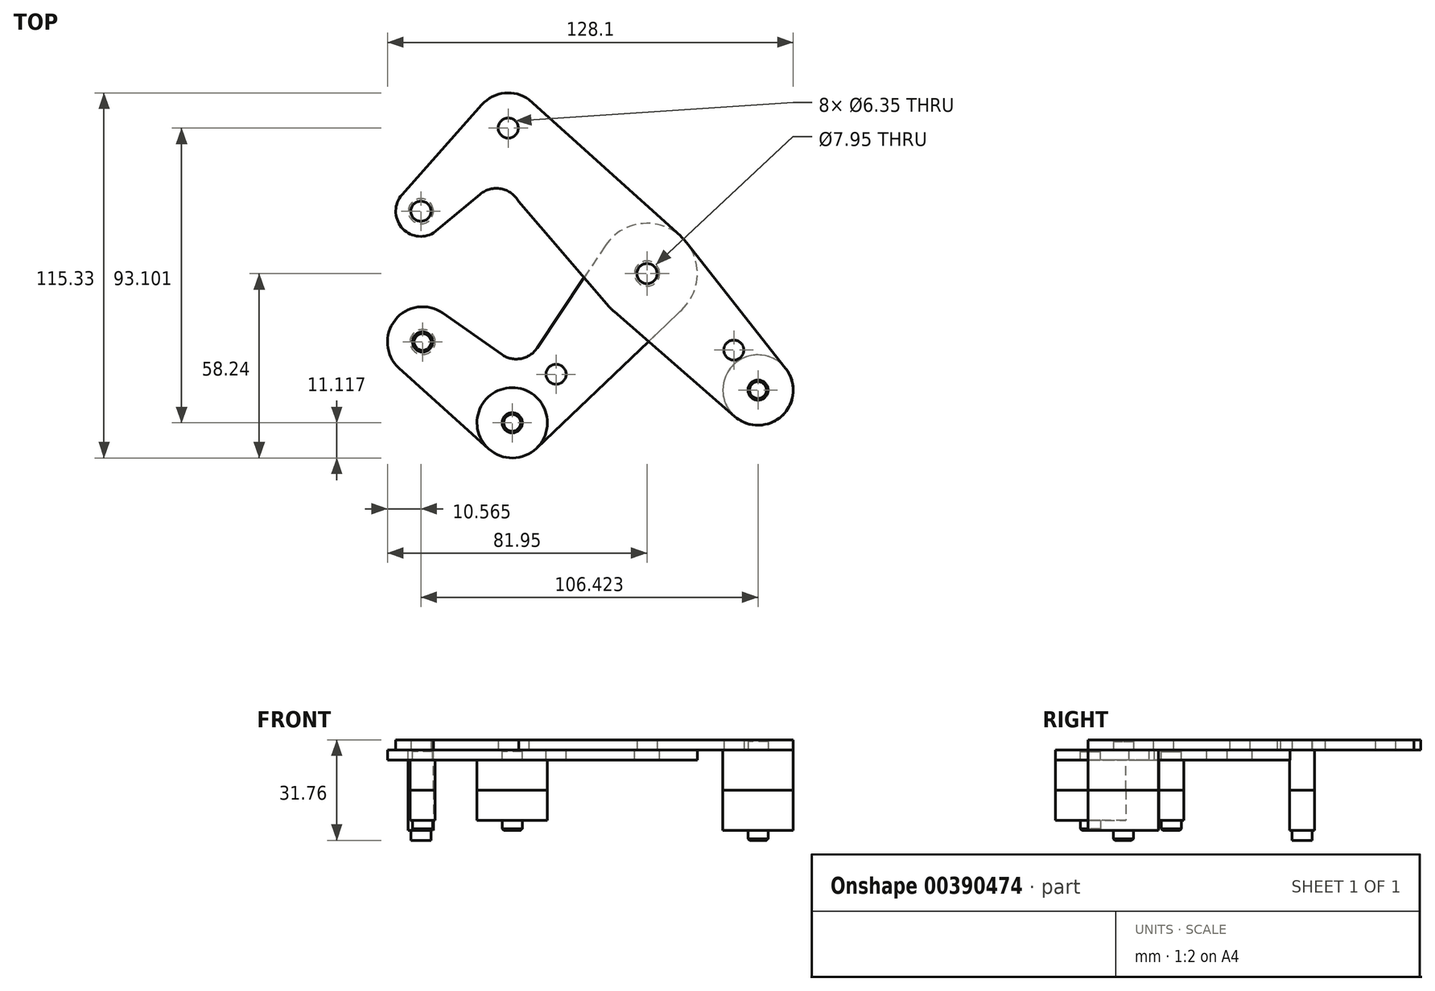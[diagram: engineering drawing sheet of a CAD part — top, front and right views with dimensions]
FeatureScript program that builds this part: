
annotation { "Feature Type Name" : "Feature", "Feature Type Description" : "" }
export const myFeature = defineFeature(function(context is Context, id is Id, definition is map)
    precondition{}
    {
        {
            var Q0;
            Q0=qCreatedBy(makeId("Top.planeOp"),FACE);
            var sketch = newSketch(context, id + "F0", { "sketchPlane" : qUnion([Q0])});
            skCircle(sketch, "E0", {"center": v(0, 0) * mm, "radius": 15.88 * mm});
            skCircle(sketch, "E1", {"center": v(0, 0) * mm, "radius": 3.18 * mm});
            skLineSegment(sketch, "E2", {"start": v(-50.22, 52.72) * mm, "end": v(58.42, -61.33) * mm, "construction": true});
            skLineSegment(sketch, "E3", {"start": v(-26.19, 62.75) * mm, "end": v(-73.55, 17.64) * mm, "construction": true});
            skCircle(sketch, "E4", {"center": v(-71.38, 19.7) * mm, "radius": 7.94 * mm});
            skCircle(sketch, "E5", {"center": v(-43.8, 45.98) * mm, "radius": 11.11 * mm});
            skCircle(sketch, "E6", {"center": v(35.04, -36.78) * mm, "radius": 11.11 * mm});
            skCircle(sketch, "E7", {"center": v(-43.8, 45.98) * mm, "radius": 3.18 * mm});
            skCircle(sketch, "E8", {"center": v(35.04, -36.78) * mm, "radius": 3.18 * mm});
            skCircle(sketch, "E9", {"center": v(-71.38, 19.7) * mm, "radius": 3.18 * mm});
            skCircle(sketch, "E10", {"center": v(0, 0) * mm, "radius": 3.98 * mm});
            skLineSegment(sketch, "E11", {"start": v(43.77, -29.9) * mm, "end": v(12.47, 9.82) * mm});
            skLineSegment(sketch, "E12", {"start": v(12.47, 9.82) * mm, "end": v(12.47, 9.82) * mm});
            skLineSegment(sketch, "E13", {"start": v(-52.1, 53.36) * mm, "end": v(-77.32, 24.97) * mm});
            skLineSegment(sketch, "E14", {"start": v(-37.25, 54.96) * mm, "end": v(10.63, 11.8) * mm});
            skLineSegment(sketch, "E15", {"start": v(-12.03, -10.36) * mm, "end": v(-40.55, 22.75) * mm});
            skLineSegment(sketch, "E16", {"start": v(-67.37, 12.85) * mm, "end": v(-52.63, 25.1) * mm});
            skArc(sketch, "E17", {"start": v(-52.63, 25.1) * mm, "mid": v(-46.04, 26.78) * mm, "end": v(-40.55, 22.75) * mm});
            skLineSegment(sketch, "E18", {"start": v(-10.42, -11.98) * mm, "end": v(27.75, -45.17) * mm});
            skLineSegment(sketch, "E19", {"start": v(0, 0) * mm, "end": v(-50.8, -56.24) * mm, "construction": true});
            skLineSegment(sketch, "E20", {"start": v(-35.24, -53.73) * mm, "end": v(-80.55, -12.81) * mm, "construction": true});
            skCircle(sketch, "E21", {"center": v(-70.84, -21.58) * mm, "radius": 3.18 * mm});
            skCircle(sketch, "E22", {"center": v(-70.84, -21.58) * mm, "radius": 11.11 * mm});
            skCircle(sketch, "E23", {"center": v(-42.56, -47.12) * mm, "radius": 3.18 * mm});
            skCircle(sketch, "E24", {"center": v(-42.56, -47.12) * mm, "radius": 11.11 * mm});
            skCircle(sketch, "E25", {"center": v(-28.72, -31.8) * mm, "radius": 3.18 * mm});
            skLineSegment(sketch, "E26", {"start": v(-64.46, -12.48) * mm, "end": v(-45.8, -25.56) * mm});
            skLineSegment(sketch, "E27", {"start": v(-79.53, -28.7) * mm, "end": v(-50.01, -55.37) * mm});
            skLineSegment(sketch, "E28", {"start": v(-34.9, -55.17) * mm, "end": v(10.95, -11.5) * mm});
            skLineSegment(sketch, "E29", {"start": v(-13.22, 8.78) * mm, "end": v(-34.62, -23.44) * mm});
            skArc(sketch, "E30", {"start": v(-45.8, -25.56) * mm, "mid": v(-39.77, -26.86) * mm, "end": v(-34.62, -23.44) * mm});
            skCircle(sketch, "E31", {"center": v(27.4, -24.16) * mm, "radius": 3.18 * mm});
            skPoint(sketch, "E31.first.point", {"position": v(25.2, -26.45) * mm});
            skPoint(sketch, "E31.second.point", {"position": v(29.75, -22.03) * mm});
            skPoint(sketch, "E31.third.point", {"position": v(30.07, -25.87) * mm});
            skSolve(sketch);
        }
        {
            var Q0;
            Q0=qCreatedBy(makeId("Top.planeOp"),FACE);
            cPlane(context, id + "F1", {"entities" : qUnion([Q0]), "cplaneType" : CPlaneType.OFFSET, "offset" : 12.7 * mm, "oppositeDirection" : true, "width" : 152.4 * mm, "height" : 152.4 * mm});
        }
        {
            var Q0;
            {var subQ0=sQuery(id+"F0.wireOp",EDGE,"E16");var subQ1=sQuery(id+"F0.wireOp",EDGE,"E4");var subQ2=makeQuery(id+"F0.imprint","INTERSECT",VERTEX,{"disambiguationData":[OD(0.0)],"derivedFrom":[subQ1,subQ0]});Q0=makeQuery(id+"F0.imprint","IMPRINT",FACE,{"disambiguationData":[TD([[makeQuery(id+"F0.imprint","IMPRINT",EDGE,{"disambiguationData":[TD([[subQ2,-1.0]])],"derivedFrom":subQ1}),1.0]])]});}
            var Q1;
            {var subQ0=sQuery(id+"F0.wireOp",EDGE,"E14");var subQ1=sQuery(id+"F0.wireOp",EDGE,"E5");var subQ2=makeQuery(id+"F0.imprint","INTERSECT",VERTEX,{"disambiguationData":[OD(0.0)],"derivedFrom":[subQ1,subQ0]});Q1=makeQuery(id+"F0.imprint","IMPRINT",FACE,{"disambiguationData":[TD([[makeQuery(id+"F0.imprint","IMPRINT",EDGE,{"disambiguationData":[TD([[subQ2,1.0]])],"derivedFrom":subQ1}),1.0]])]});}
            var Q2;
            Q2=makeQuery(id+"F0.imprint","IMPRINT",FACE,{"disambiguationData":[TD([[makeQuery(id+"F0.imprint","IMPRINT",EDGE,{"derivedFrom":sQuery(id+"F0.wireOp",EDGE,"E8")}),-1.0]])]});
            var Q3;
            {var subQ0=sQuery(id+"F0.wireOp",EDGE,"E15");var subQ1=sQuery(id+"F0.wireOp",EDGE,"E0");var subQ2=makeQuery(id+"F0.imprint","INTERSECT",VERTEX,{"derivedFrom":[subQ1,subQ0]});Q3=makeQuery(id+"F0.imprint","IMPRINT",FACE,{"disambiguationData":[TD([[makeQuery(id+"F0.imprint","IMPRINT",EDGE,{"disambiguationData":[TD([[subQ2,1.0]])],"derivedFrom":subQ1}),-1.0]])]});}
            var Q4;
            {var subQ0=sQuery(id+"F0.wireOp",EDGE,"E18");var subQ1=sQuery(id+"F0.wireOp",EDGE,"E0");var subQ2=makeQuery(id+"F0.imprint","INTERSECT",VERTEX,{"derivedFrom":[subQ1,subQ0]});Q4=makeQuery(id+"F0.imprint","IMPRINT",FACE,{"disambiguationData":[TD([[makeQuery(id+"F0.imprint","IMPRINT",EDGE,{"disambiguationData":[TD([[subQ2,-1.0]])],"derivedFrom":subQ1}),-1.0]])]});}
            var Q5;
            Q5=makeQuery(id+"F0.imprint","IMPRINT",FACE,{"disambiguationData":[TD([[makeQuery(id+"F0.imprint","IMPRINT",EDGE,{"derivedFrom":sQuery(id+"F0.wireOp",EDGE,"E9")}),-1.0]])]});
            var Q6;
            Q6=makeQuery(id+"F0.imprint","IMPRINT",FACE,{"disambiguationData":[TD([[makeQuery(id+"F0.imprint","IMPRINT",EDGE,{"derivedFrom":sQuery(id+"F0.wireOp",EDGE,"E7")}),-1.0]])]});
            var Q7;
            {var subQ0=sQuery(id+"F0.wireOp",EDGE,"E13");Q7=makeQuery(id+"F0.imprint","IMPRINT",FACE,{"disambiguationData":[TD([[makeQuery(id+"F0.imprint","IMPRINT",EDGE,{"derivedFrom":subQ0}),1.0]])]});}
            var Q8;
            {var subQ7=sQuery(id+"F0.wireOp",EDGE,"E11");Q8=makeQuery(id+"F0.imprint","IMPRINT",FACE,{"disambiguationData":[TD([[makeQuery(id+"F0.imprint","IMPRINT",EDGE,{"derivedFrom":subQ7}),1.0]])]});}
            var Q9;
            Q9=makeQuery(id+"F0.imprint","IMPRINT",FACE,{"disambiguationData":[TD([[makeQuery(id+"F0.imprint","IMPRINT",EDGE,{"derivedFrom":sQuery(id+"F0.wireOp",EDGE,"E10")}),-1.0]])]});
            var Q10;
            Q10=makeQuery(id+"F0.imprint","IMPRINT",FACE,{"disambiguationData":[TD([[makeQuery(id+"F0.imprint","IMPRINT",EDGE,{"derivedFrom":sQuery(id+"F0.wireOp",EDGE,"E1")}),-1.0]])]});
            extrude(context, id + "F2", {"entities" : qUnion([Q0, Q1, Q2, Q3, Q4, Q5, Q6, Q7, Q8, Q9, Q10]), "depth" : 3.17 * mm});
        }
        {
            var Q0;
            Q0=makeQuery(id+"F0.imprint","IMPRINT",FACE,{"disambiguationData":[TD([[makeQuery(id+"F0.imprint","IMPRINT",EDGE,{"derivedFrom":sQuery(id+"F0.wireOp",EDGE,"E21")}),-1.0]])]});
            var Q1;
            Q1=makeQuery(id+"F0.imprint","IMPRINT",FACE,{"disambiguationData":[TD([[makeQuery(id+"F0.imprint","IMPRINT",EDGE,{"derivedFrom":sQuery(id+"F0.wireOp",EDGE,"E25")}),-1.0]])]});
            var Q2;
            Q2=makeQuery(id+"F0.imprint","IMPRINT",FACE,{"disambiguationData":[TD([[makeQuery(id+"F0.imprint","IMPRINT",EDGE,{"derivedFrom":sQuery(id+"F0.wireOp",EDGE,"E23")}),-1.0]])]});
            var Q3;
            {var subQ0=sQuery(id+"F0.wireOp",EDGE,"E18");var subQ1=sQuery(id+"F0.wireOp",EDGE,"E0");var subQ2=makeQuery(id+"F0.imprint","INTERSECT",VERTEX,{"derivedFrom":[subQ1,subQ0]});Q3=makeQuery(id+"F0.imprint","IMPRINT",FACE,{"disambiguationData":[TD([[makeQuery(id+"F0.imprint","IMPRINT",EDGE,{"disambiguationData":[TD([[subQ2,-1.0]])],"derivedFrom":subQ1}),-1.0]])]});}
            var Q4;
            {var subQ0=sQuery(id+"F0.wireOp",EDGE,"E15");var subQ1=sQuery(id+"F0.wireOp",EDGE,"E0");var subQ2=makeQuery(id+"F0.imprint","INTERSECT",VERTEX,{"derivedFrom":[subQ1,subQ0]});Q4=makeQuery(id+"F0.imprint","IMPRINT",FACE,{"disambiguationData":[TD([[makeQuery(id+"F0.imprint","IMPRINT",EDGE,{"disambiguationData":[TD([[subQ2,1.0]])],"derivedFrom":subQ1}),-1.0]])]});}
            var Q5;
            Q5=makeQuery(id+"F0.imprint","IMPRINT",FACE,{"disambiguationData":[TD([[makeQuery(id+"F0.imprint","IMPRINT",EDGE,{"derivedFrom":sQuery(id+"F0.wireOp",EDGE,"E10")}),-1.0]])]});
            extrude(context, id + "F3", {"entities" : qUnion([Q0, Q1, Q2, Q3, Q4, Q5]), "oppositeDirection" : true, "depth" : 3.17 * mm});
        }
        {
            var Q0;
            Q0=makeQuery(id+"F2.opExtrude","CAP_FACE",FACE,{"disambiguationData":[OSD([sQuery(id+"F0.wireOp",EDGE,"E0"),sQuery(id+"F0.wireOp",EDGE,"E1"),sQuery(id+"F0.wireOp",EDGE,"E4"),sQuery(id+"F0.wireOp",EDGE,"E5"),sQuery(id+"F0.wireOp",EDGE,"E6"),sQuery(id+"F0.wireOp",EDGE,"E7"),sQuery(id+"F0.wireOp",EDGE,"E8"),sQuery(id+"F0.wireOp",EDGE,"E9"),sQuery(id+"F0.wireOp",EDGE,"E11"),sQuery(id+"F0.wireOp",EDGE,"E13"),sQuery(id+"F0.wireOp",EDGE,"E14"),sQuery(id+"F0.wireOp",EDGE,"E15"),sQuery(id+"F0.wireOp",EDGE,"E16"),sQuery(id+"F0.wireOp",EDGE,"E17"),sQuery(id+"F0.wireOp",EDGE,"E18"),sQuery(id+"F0.wireOp",EDGE,"E31")])],"isStart":false});
            var sketch = newSketch(context, id + "F4", { "sketchPlane" : qUnion([Q0])});
            skCircle(sketch, "E32", {"center": v(35.04, -36.78) * mm, "radius": 11.11 * mm});
            skCircle(sketch, "E33", {"center": v(-71.38, 19.7) * mm, "radius": 3.96 * mm});
            skSolve(sketch);
        }
        {
            var Q0;
            Q0=makeQuery(id+"F3.opExtrude","CAP_FACE",FACE,{"disambiguationData":[OSD([sQuery(id+"F0.wireOp",EDGE,"E0"),sQuery(id+"F0.wireOp",EDGE,"E10"),sQuery(id+"F0.wireOp",EDGE,"E21"),sQuery(id+"F0.wireOp",EDGE,"E22"),sQuery(id+"F0.wireOp",EDGE,"E23"),sQuery(id+"F0.wireOp",EDGE,"E24"),sQuery(id+"F0.wireOp",EDGE,"E25"),sQuery(id+"F0.wireOp",EDGE,"E26"),sQuery(id+"F0.wireOp",EDGE,"E27"),sQuery(id+"F0.wireOp",EDGE,"E28"),sQuery(id+"F0.wireOp",EDGE,"E29"),sQuery(id+"F0.wireOp",EDGE,"E30")])],"isStart":true});
            var sketch = newSketch(context, id + "F5", { "sketchPlane" : qUnion([Q0])});
            skCircle(sketch, "E34", {"center": v(-42.56, -47.12) * mm, "radius": 11.11 * mm});
            skCircle(sketch, "E35", {"center": v(-70.84, -21.58) * mm, "radius": 3.96 * mm});
            skSolve(sketch);
        }
        {
            var Q0;
            Q0 = qSketchRegion(id + "F5", true);
            var Q1;
            Q1 = qSketchRegion(id + "F4", true);
            var Q2;
            Q2=qCreatedBy(id+"F1.planeOp",FACE);
            extrude(context, id + "F6", {"entities" : qUnion([Q0, Q1]), "endBound" : BoundingType.UP_TO_SURFACE, "oppositeDirection" : true, "endBoundEntityFace" : qUnion([Q2]), "depth" : 10.92 * mm});
        }
        {
            var Q0;
            Q0=makeQuery(id+"F2.opExtrude","SWEPT_BODY",BODY,{"disambiguationData":[OSD([sQuery(id+"F0.wireOp",EDGE,"E0"),sQuery(id+"F0.wireOp",EDGE,"E1"),sQuery(id+"F0.wireOp",EDGE,"E4"),sQuery(id+"F0.wireOp",EDGE,"E5"),sQuery(id+"F0.wireOp",EDGE,"E6"),sQuery(id+"F0.wireOp",EDGE,"E7"),sQuery(id+"F0.wireOp",EDGE,"E8"),sQuery(id+"F0.wireOp",EDGE,"E9"),sQuery(id+"F0.wireOp",EDGE,"E11"),sQuery(id+"F0.wireOp",EDGE,"E13"),sQuery(id+"F0.wireOp",EDGE,"E14"),sQuery(id+"F0.wireOp",EDGE,"E15"),sQuery(id+"F0.wireOp",EDGE,"E16"),sQuery(id+"F0.wireOp",EDGE,"E17"),sQuery(id+"F0.wireOp",EDGE,"E18"),sQuery(id+"F0.wireOp",EDGE,"E31")])]});
            var Q1;
            Q1=makeQuery(id+"F3.opExtrude","SWEPT_BODY",BODY,{"disambiguationData":[OSD([sQuery(id+"F0.wireOp",EDGE,"E0"),sQuery(id+"F0.wireOp",EDGE,"E10"),sQuery(id+"F0.wireOp",EDGE,"E21"),sQuery(id+"F0.wireOp",EDGE,"E22"),sQuery(id+"F0.wireOp",EDGE,"E23"),sQuery(id+"F0.wireOp",EDGE,"E24"),sQuery(id+"F0.wireOp",EDGE,"E25"),sQuery(id+"F0.wireOp",EDGE,"E26"),sQuery(id+"F0.wireOp",EDGE,"E27"),sQuery(id+"F0.wireOp",EDGE,"E28"),sQuery(id+"F0.wireOp",EDGE,"E29"),sQuery(id+"F0.wireOp",EDGE,"E30")])]});
            var Q2;
            Q2=makeQuery(id+"F6.opExtrude","SWEPT_BODY",BODY,{"disambiguationData":[OSD([sQuery(id+"F4.wireOp",EDGE,"E32")])]});
            var Q3;
            Q3=makeQuery(id+"F6.opExtrude","SWEPT_BODY",BODY,{"disambiguationData":[OSD([sQuery(id+"F4.wireOp",EDGE,"E33")])]});
            var Q4;
            Q4=makeQuery(id+"F6.opExtrude","SWEPT_BODY",BODY,{"disambiguationData":[OSD([sQuery(id+"F5.wireOp",EDGE,"E34")])]});
            var Q5;
            Q5=makeQuery(id+"F6.opExtrude","SWEPT_BODY",BODY,{"disambiguationData":[OSD([sQuery(id+"F5.wireOp",EDGE,"E35")])]});
            booleanBodies(context, id + "F7", {"operationType" : BooleanOperationType.SUBTRACTION, "tools" : qUnion([Q0, Q1]), "targets" : qUnion([Q2, Q3, Q4, Q5]), "keepTools" : true});
        }
        {
            var Q0;
            Q0=makeQuery(id+"F6.opExtrude","CAP_FACE",FACE,{"disambiguationData":[OSD([sQuery(id+"F5.wireOp",EDGE,"E35")])],"isStart":true});
            var Q1;
            Q1=makeQuery(id+"F6.opExtrude","CAP_FACE",FACE,{"disambiguationData":[OSD([sQuery(id+"F5.wireOp",EDGE,"E34")])],"isStart":true});
            var Q2;
            Q2=makeQuery(id+"F6.opExtrude","CAP_FACE",FACE,{"disambiguationData":[OSD([sQuery(id+"F4.wireOp",EDGE,"E32")])],"isStart":true});
            var Q3;
            Q3=makeQuery(id+"F7.opBoolean","COPY",EDGE,{"derivedFrom":makeQuery(id+"F2.opExtrude","CAP_EDGE",EDGE,{"disambiguationData":[OSD([sQuery(id+"F0.wireOp",EDGE,"E9")])],"isStart":false})});
            chamfer(context, id + "F8", {"entities" : qUnion([Q0, Q1, Q2, Q3]), "width" : 0.5 * mm, "tangentPropagation" : true});
        }
        {
            var Q0;
            Q0=makeQuery(id+"F6.opExtrude","SWEPT_BODY",BODY,{"disambiguationData":[OSD([sQuery(id+"F4.wireOp",EDGE,"E33")])]});
            var Q1;
            Q1=makeQuery(id+"F6.opExtrude","SWEPT_BODY",BODY,{"disambiguationData":[OSD([sQuery(id+"F4.wireOp",EDGE,"E32")])]});
            var Q2;
            Q2=makeQuery(id+"F6.opExtrude","SWEPT_BODY",BODY,{"disambiguationData":[OSD([sQuery(id+"F5.wireOp",EDGE,"E34")])]});
            var Q3;
            Q3=makeQuery(id+"F6.opExtrude","SWEPT_BODY",BODY,{"disambiguationData":[OSD([sQuery(id+"F5.wireOp",EDGE,"E35")])]});
            var Q4;
            Q4=qCreatedBy(id+"F1.planeOp",FACE);
            mirror(context, id + "F9", {"entities" : qUnion([Q0, Q1, Q2, Q3]), "mirrorPlane" : qUnion([Q4])});
        }
    });
